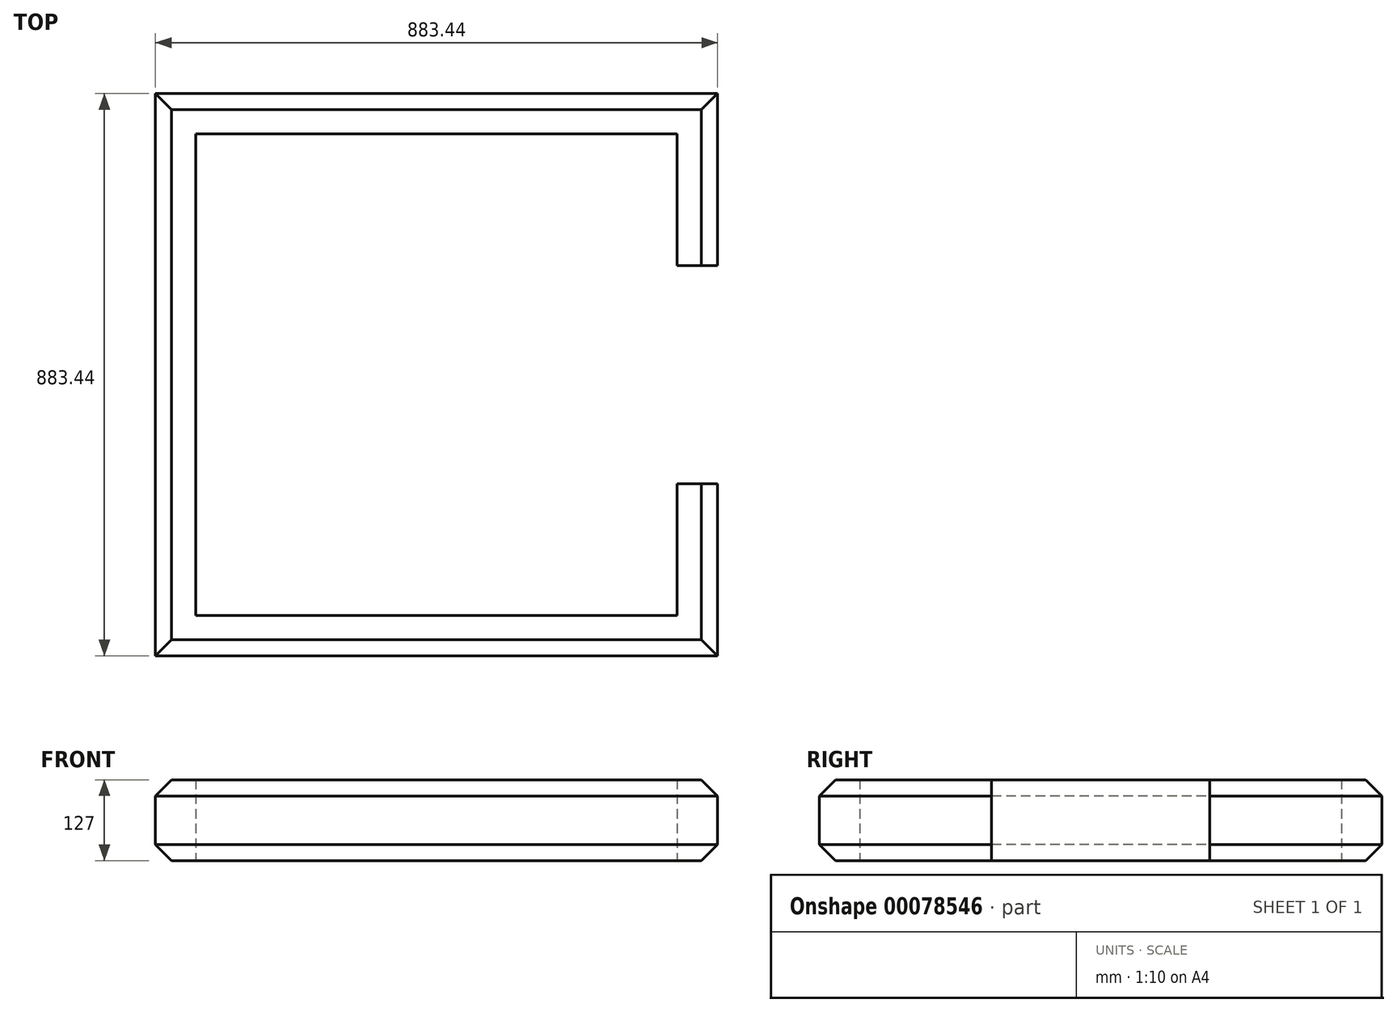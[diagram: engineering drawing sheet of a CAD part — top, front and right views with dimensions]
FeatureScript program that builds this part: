
annotation { "Feature Type Name" : "Feature", "Feature Type Description" : "" }
export const myFeature = defineFeature(function(context is Context, id is Id, definition is map)
    precondition{}
    {
        {
            var Q0;
            Q0=qCreatedBy(makeId("Front.planeOp"),FACE);
            var sketch = newSketch(context, id + "F0", { "sketchPlane" : qUnion([Q0])});
            skLineSegment(sketch, "E0", {"start": v(-38.1, 63.5) * mm, "end": v(0, 63.5) * mm});
            skLineSegment(sketch, "E1", {"start": v(-38.1, -63.5) * mm, "end": v(0, -63.5) * mm});
            skLineSegment(sketch, "E2", {"start": v(25.4, 0) * mm, "end": v(25.4, 38.1) * mm});
            skLineSegment(sketch, "E3", {"start": v(25.4, 0) * mm, "end": v(25.4, -38.1) * mm});
            skLineSegment(sketch, "E4", {"start": v(0, 63.5) * mm, "end": v(25.4, 38.1) * mm});
            skLineSegment(sketch, "E5", {"start": v(25.4, -38.1) * mm, "end": v(0, -63.5) * mm});
            skLineSegment(sketch, "E6", {"start": v(-38.1, 63.5) * mm, "end": v(-38.1, -63.5) * mm});
            skLineSegment(sketch, "E7", {"start": v(-38.1, 0) * mm, "end": v(-38.1, 63.5) * mm});
            skLineSegment(sketch, "E8", {"start": v(-38.1, 0) * mm, "end": v(-38.1, -63.5) * mm});
            skSolve(sketch);
        }
        {
            var Q0;
            Q0=qCreatedBy(makeId("Top.planeOp"),FACE);
            var sketch = newSketch(context, id + "F1", { "sketchPlane" : qUnion([Q0])});
            skLineSegment(sketch, "E9", {"start": v(-41.67, 0) * mm, "end": v(-41.67, 203.2) * mm});
            skLineSegment(sketch, "E10", {"start": v(-41.67, 203.2) * mm, "end": v(-790.97, 203.2) * mm});
            skLineSegment(sketch, "E11", {"start": v(-790.97, 203.2) * mm, "end": v(-790.97, -546.1) * mm});
            skLineSegment(sketch, "E12", {"start": v(-790.97, -546.1) * mm, "end": v(-41.67, -546.1) * mm});
            skLineSegment(sketch, "E13", {"start": v(-41.67, -546.1) * mm, "end": v(-41.67, -342.9) * mm});
            skSolve(sketch);
        }
        {
            var Q0;
            Q0=makeQuery(id+"F0.imprint","IMPRINT",FACE,{"disambiguationData":[TD([[makeQuery(id+"F0.imprint","IMPRINT",EDGE,{"derivedFrom":sQuery(id+"F0.wireOp",EDGE,"E0")}),-1.0]])]});
            var Q1;
            Q1 = qConstructionFilter(qBodyType(qCreatedBy(id + "F1" ,EDGE), BodyType.WIRE), ConstructionObject.NO);
            sweep(context, id + "F2", {"profiles" : qUnion([Q0]), "path" : qUnion([Q1])});
        }
    });
